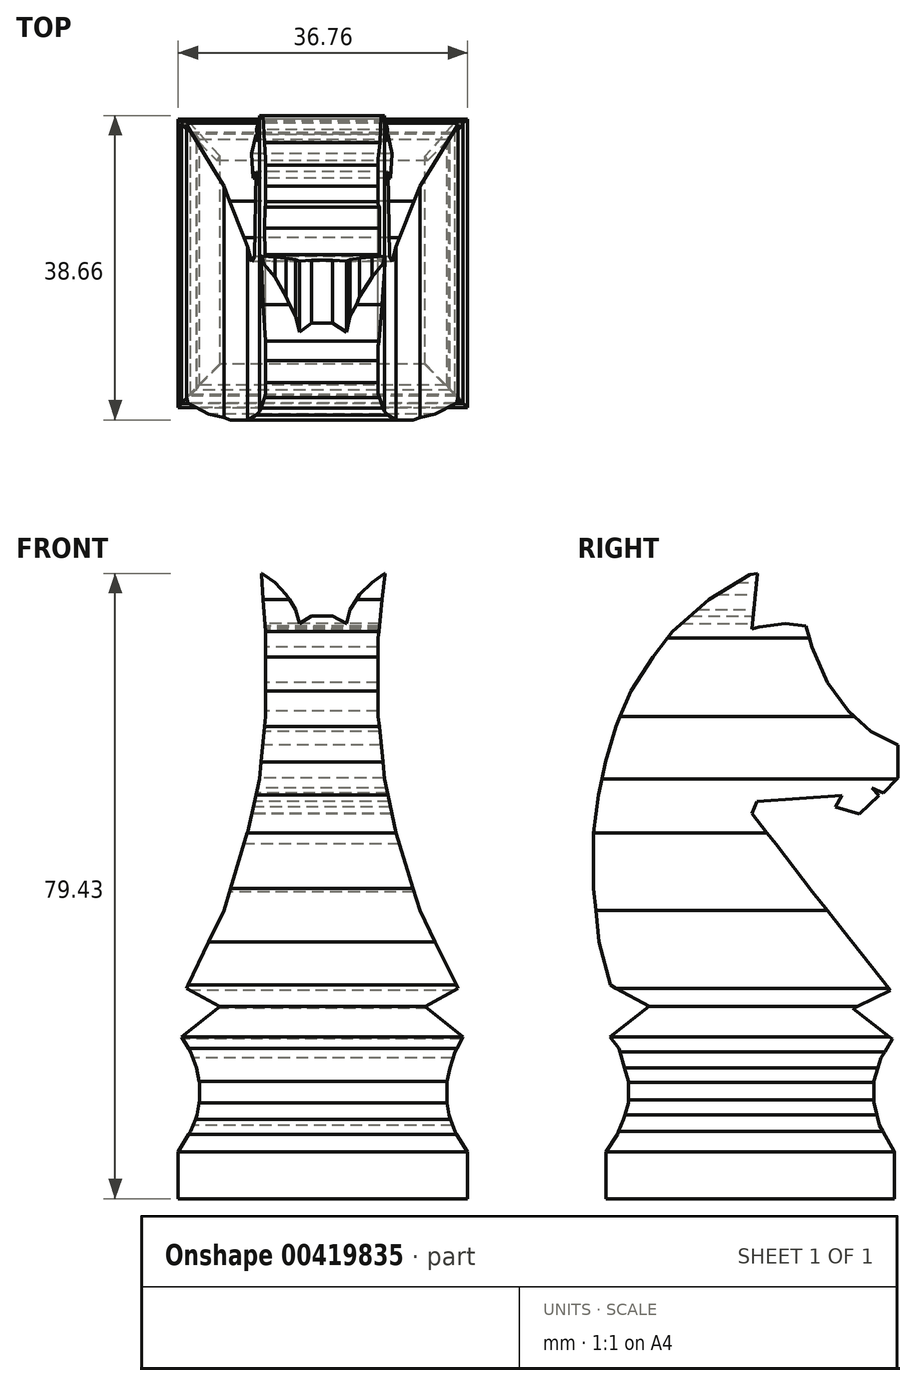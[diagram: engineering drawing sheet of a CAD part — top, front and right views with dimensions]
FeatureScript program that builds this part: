
annotation { "Feature Type Name" : "Feature", "Feature Type Description" : "" }
export const myFeature = defineFeature(function(context is Context, id is Id, definition is map)
    precondition{}
    {
        {
            var Q0;
            Q0=qCreatedBy(makeId("Front.planeOp"),FACE);
            var sketch = newSketch(context, id + "F0", { "sketchPlane" : qUnion([Q0])});
            skSolve(sketch);
        }
        {
            var Q0;
            Q0=qCreatedBy(makeId("Right.planeOp"),FACE);
            var sketch = newSketch(context, id + "F1", { "sketchPlane" : qUnion([Q0])});
            skSolve(sketch);
        }
        {
            var Q0;
            Q0=qCreatedBy(makeId("Right.planeOp"),FACE);
            var sketch = newSketch(context, id + "F2", { "sketchPlane" : qUnion([Q0])});
            skLineSegment(sketch, "E0.bottom", {"start": v(21.59, 43.18) * mm, "end": v(-21.6, 43.18) * mm});
            skLineSegment(sketch, "E0.top", {"start": v(21.6, -43.18) * mm, "end": v(-21.59, -43.18) * mm});
            skLineSegment(sketch, "E0.left", {"start": v(21.59, 43.18) * mm, "end": v(21.6, -43.18) * mm});
            skLineSegment(sketch, "E0.right", {"start": v(-21.6, 43.18) * mm, "end": v(-21.59, -43.18) * mm});
            skSolve(sketch);
        }
        {
            var Q0;
            Q0 = qSketchRegion(id + "F2", true);
            extrude(context, id + "F3", {"entities" : qUnion([Q0]), "endBound" : BoundingType.SYMMETRIC, "depth" : 43.18 * mm});
        }
        {
            var Q0;
            Q0=makeQuery(id+"F3.opExtrude","SWEPT_FACE",FACE,{"disambiguationData":[OSD([sQuery(id+"F2.wireOp",EDGE,"E0.left")])]});
            var sketch = newSketch(context, id + "F4", { "sketchPlane" : qUnion([Q0])});
            skLineSegment(sketch, "E1", {"start": v(-21.59, -43.18) * mm, "end": v(21.59, -43.18) * mm});
            skLineSegment(sketch, "E2", {"start": v(21.59, -43.18) * mm, "end": v(21.59, 43.18) * mm});
            skLineSegment(sketch, "E3", {"start": v(21.59, 43.18) * mm, "end": v(-21.59, 43.18) * mm});
            skLineSegment(sketch, "E4", {"start": v(-21.59, 43.18) * mm, "end": v(-21.59, -43.18) * mm});
            skLineSegment(sketch, "E5", {"start": v(-18.46, -40.66) * mm, "end": v(18.3, -40.66) * mm});
            skLineSegment(sketch, "E6", {"start": v(18.3, -40.66) * mm, "end": v(18.3, -34.69) * mm});
            skLineSegment(sketch, "E7", {"start": v(18.3, -34.69) * mm, "end": v(16.76, -32.12) * mm});
            skLineSegment(sketch, "E8", {"start": v(16.76, -32.12) * mm, "end": v(15.89, -30.04) * mm});
            skLineSegment(sketch, "E9", {"start": v(15.89, -30.04) * mm, "end": v(15.6, -28.1) * mm});
            skLineSegment(sketch, "E10", {"start": v(15.6, -28.1) * mm, "end": v(15.6, -25.91) * mm});
            skLineSegment(sketch, "E11", {"start": v(15.6, -25.91) * mm, "end": v(15.99, -24.03) * mm});
            skLineSegment(sketch, "E12", {"start": v(15.99, -24.03) * mm, "end": v(16.73, -22) * mm});
            skLineSegment(sketch, "E13", {"start": v(16.73, -22) * mm, "end": v(17.9, -20.1) * mm});
            skLineSegment(sketch, "E14", {"start": v(17.9, -20.1) * mm, "end": v(13.01, -16.24) * mm});
            skLineSegment(sketch, "E15", {"start": v(13.01, -16.24) * mm, "end": v(17.27, -13.92) * mm});
            skLineSegment(sketch, "E16", {"start": v(17.27, -13.92) * mm, "end": v(12.51, -4.06) * mm});
            skLineSegment(sketch, "E17", {"start": v(12.51, -4.06) * mm, "end": v(9.52, 5.8) * mm});
            skLineSegment(sketch, "E18", {"start": v(9.52, 5.8) * mm, "end": v(7.96, 12.63) * mm});
            skLineSegment(sketch, "E19", {"start": v(7.96, 12.63) * mm, "end": v(7.18, 20.62) * mm});
            skLineSegment(sketch, "E20", {"start": v(7.18, 20.62) * mm, "end": v(7.18, 30.56) * mm});
            skLineSegment(sketch, "E21", {"start": v(7.18, 30.56) * mm, "end": v(7.74, 38.8) * mm});
            skLineSegment(sketch, "E22", {"start": v(7.74, 38.8) * mm, "end": v(5.98, 37.6) * mm});
            skLineSegment(sketch, "E23", {"start": v(5.98, 37.6) * mm, "end": v(4.59, 36.11) * mm});
            skLineSegment(sketch, "E24", {"start": v(4.59, 36.11) * mm, "end": v(3.38, 34.2) * mm});
            skLineSegment(sketch, "E25", {"start": v(3.38, 34.2) * mm, "end": v(2.9, 32.38) * mm});
            skLineSegment(sketch, "E26", {"start": v(2.9, 32.38) * mm, "end": v(1.37, 33.38) * mm});
            skLineSegment(sketch, "E27", {"start": v(1.37, 33.38) * mm, "end": v(-1.3, 33.38) * mm});
            skLineSegment(sketch, "E28", {"start": v(-1.3, 33.38) * mm, "end": v(-3.05, 32.38) * mm});
            skLineSegment(sketch, "E29", {"start": v(-3.05, 32.38) * mm, "end": v(-3.53, 34.2) * mm});
            skLineSegment(sketch, "E30", {"start": v(-3.53, 34.2) * mm, "end": v(-4.7, 36.11) * mm});
            skLineSegment(sketch, "E31", {"start": v(-4.7, 36.11) * mm, "end": v(-6.3, 37.6) * mm});
            skLineSegment(sketch, "E32", {"start": v(-6.3, 37.6) * mm, "end": v(-7.95, 38.8) * mm});
            skLineSegment(sketch, "E33", {"start": v(-7.95, 38.8) * mm, "end": v(-7.1, 30.56) * mm});
            skLineSegment(sketch, "E34", {"start": v(-7.1, 30.56) * mm, "end": v(-7.1, 20.62) * mm});
            skLineSegment(sketch, "E35", {"start": v(-7.1, 20.62) * mm, "end": v(-7.92, 12.63) * mm});
            skLineSegment(sketch, "E36", {"start": v(-7.92, 12.63) * mm, "end": v(-9.38, 5.8) * mm});
            skLineSegment(sketch, "E37", {"start": v(-9.38, 5.8) * mm, "end": v(-12.4, -4.06) * mm});
            skLineSegment(sketch, "E38", {"start": v(-12.4, -4.06) * mm, "end": v(-17.2, -13.92) * mm});
            skLineSegment(sketch, "E39", {"start": v(-17.2, -13.92) * mm, "end": v(-13.05, -16.24) * mm});
            skLineSegment(sketch, "E40", {"start": v(-13.05, -16.24) * mm, "end": v(-17.89, -20.1) * mm});
            skLineSegment(sketch, "E41", {"start": v(-17.89, -20.1) * mm, "end": v(-16.85, -22) * mm});
            skLineSegment(sketch, "E42", {"start": v(-16.85, -22) * mm, "end": v(-16.2, -24.03) * mm});
            skLineSegment(sketch, "E43", {"start": v(-16.2, -24.03) * mm, "end": v(-15.8, -25.91) * mm});
            skLineSegment(sketch, "E44", {"start": v(-15.8, -25.91) * mm, "end": v(-15.8, -28.1) * mm});
            skLineSegment(sketch, "E45", {"start": v(-15.8, -28.1) * mm, "end": v(-16.07, -30.04) * mm});
            skLineSegment(sketch, "E46", {"start": v(-16.07, -30.04) * mm, "end": v(-16.83, -32.12) * mm});
            skLineSegment(sketch, "E47", {"start": v(-16.83, -32.12) * mm, "end": v(-18.44, -34.69) * mm});
            skLineSegment(sketch, "E48", {"start": v(-18.44, -34.69) * mm, "end": v(-18.46, -40.66) * mm});
            skSolve(sketch);
        }
        {
            var Q0;
            Q0=makeQuery(id+"F4.imprint","IMPRINT",FACE,{"disambiguationData":[TD([[makeQuery(id+"F4.imprint","IMPRINT",EDGE,{"derivedFrom":sQuery(id+"F4.wireOp",EDGE,"E1")}),1.0]])]});
            extrude(context, id + "F5", {"entities" : qUnion([Q0]), "operationType" : NewBodyOperationType.REMOVE, "oppositeDirection" : true, "depth" : 43.18 * mm});
        }
        {
            var Q0;
            Q0=qCreatedBy(makeId("Right.planeOp"),FACE);
            var sketch = newSketch(context, id + "F6", { "sketchPlane" : qUnion([Q0])});
            skLineSegment(sketch, "E49", {"start": v(22.04, -40.82) * mm, "end": v(18.95, -40.82) * mm});
            skLineSegment(sketch, "E50", {"start": v(18.95, -40.82) * mm, "end": v(18.95, -34.69) * mm});
            skLineSegment(sketch, "E51", {"start": v(18.95, -34.69) * mm, "end": v(17.04, -31.36) * mm});
            skLineSegment(sketch, "E52", {"start": v(17.04, -31.36) * mm, "end": v(16.36, -28.41) * mm});
            skLineSegment(sketch, "E53", {"start": v(16.36, -28.41) * mm, "end": v(16.36, -25.69) * mm});
            skLineSegment(sketch, "E54", {"start": v(16.36, -25.69) * mm, "end": v(17.25, -22.75) * mm});
            skLineSegment(sketch, "E55", {"start": v(17.25, -22.75) * mm, "end": v(18.7, -20.4) * mm});
            skLineSegment(sketch, "E56", {"start": v(18.7, -20.4) * mm, "end": v(13.68, -16.51) * mm});
            skLineSegment(sketch, "E57", {"start": v(13.68, -16.51) * mm, "end": v(18.45, -14.18) * mm});
            skLineSegment(sketch, "E58", {"start": v(18.45, -14.18) * mm, "end": v(12.48, -6.63) * mm});
            skLineSegment(sketch, "E59", {"start": v(12.48, -6.63) * mm, "end": v(8.52, -1.68) * mm});
            skLineSegment(sketch, "E60", {"start": v(8.52, -1.68) * mm, "end": v(3.89, 4.38) * mm});
            skLineSegment(sketch, "E61", {"start": v(3.89, 4.38) * mm, "end": v(0.83, 8.24) * mm});
            skLineSegment(sketch, "E62", {"start": v(0.83, 8.24) * mm, "end": v(1.45, 9.81) * mm});
            skLineSegment(sketch, "E63", {"start": v(1.45, 9.81) * mm, "end": v(12.28, 10.55) * mm});
            skLineSegment(sketch, "E64", {"start": v(12.28, 10.55) * mm, "end": v(11.47, 9.1) * mm});
            skLineSegment(sketch, "E65", {"start": v(11.47, 9.1) * mm, "end": v(14.53, 8.23) * mm});
            skLineSegment(sketch, "E66", {"start": v(14.53, 8.23) * mm, "end": v(16.98, 10.58) * mm});
            skLineSegment(sketch, "E67", {"start": v(16.98, 10.58) * mm, "end": v(16.07, 11.53) * mm});
            skLineSegment(sketch, "E68", {"start": v(16.07, 11.53) * mm, "end": v(17.57, 10.85) * mm});
            skLineSegment(sketch, "E69", {"start": v(17.57, 10.85) * mm, "end": v(19.39, 12.78) * mm});
            skLineSegment(sketch, "E70", {"start": v(19.39, 12.78) * mm, "end": v(19.39, 16.97) * mm});
            skLineSegment(sketch, "E71", {"start": v(19.39, 16.97) * mm, "end": v(15.96, 18.72) * mm});
            skLineSegment(sketch, "E72", {"start": v(15.96, 18.72) * mm, "end": v(13.1, 21.3) * mm});
            skLineSegment(sketch, "E73", {"start": v(13.1, 21.3) * mm, "end": v(10.42, 24.93) * mm});
            skLineSegment(sketch, "E74", {"start": v(10.42, 24.93) * mm, "end": v(8.47, 29.44) * mm});
            skLineSegment(sketch, "E75", {"start": v(8.47, 29.44) * mm, "end": v(7.73, 32.1) * mm});
            skLineSegment(sketch, "E76", {"start": v(7.73, 32.1) * mm, "end": v(5.08, 32.39) * mm});
            skLineSegment(sketch, "E77", {"start": v(5.08, 32.39) * mm, "end": v(1.72, 31.96) * mm});
            skLineSegment(sketch, "E78", {"start": v(1.72, 31.96) * mm, "end": v(0.87, 31.73) * mm});
            skLineSegment(sketch, "E79", {"start": v(0.87, 31.73) * mm, "end": v(1.53, 38.77) * mm});
            skLineSegment(sketch, "E80", {"start": v(1.53, 38.77) * mm, "end": v(0.57, 38.63) * mm});
            skLineSegment(sketch, "E81", {"start": v(0.57, 38.63) * mm, "end": v(-4.64, 35.47) * mm});
            skLineSegment(sketch, "E82", {"start": v(-4.64, 35.47) * mm, "end": v(-9.25, 31.4) * mm});
            skLineSegment(sketch, "E83", {"start": v(-9.25, 31.4) * mm, "end": v(-11.72, 28.13) * mm});
            skLineSegment(sketch, "E84", {"start": v(-11.72, 28.13) * mm, "end": v(-14.5, 23.83) * mm});
            skLineSegment(sketch, "E85", {"start": v(-14.5, 23.83) * mm, "end": v(-16.46, 19.35) * mm});
            skLineSegment(sketch, "E86", {"start": v(-16.46, 19.35) * mm, "end": v(-17.76, 14.79) * mm});
            skLineSegment(sketch, "E87", {"start": v(-17.76, 14.79) * mm, "end": v(-18.65, 10.64) * mm});
            skLineSegment(sketch, "E88", {"start": v(-18.65, 10.64) * mm, "end": v(-19.27, 5.77) * mm});
            skLineSegment(sketch, "E89", {"start": v(-19.27, 5.77) * mm, "end": v(-19.27, -1.27) * mm});
            skLineSegment(sketch, "E90", {"start": v(-19.27, -1.27) * mm, "end": v(-18.56, -8.03) * mm});
            skLineSegment(sketch, "E91", {"start": v(-18.56, -8.03) * mm, "end": v(-17.11, -13.53) * mm});
            skLineSegment(sketch, "E92", {"start": v(-17.11, -13.53) * mm, "end": v(-12.2, -16.21) * mm});
            skLineSegment(sketch, "E93", {"start": v(-12.2, -16.21) * mm, "end": v(-17.2, -20.09) * mm});
            skLineSegment(sketch, "E94", {"start": v(-17.2, -20.09) * mm, "end": v(-16.06, -21.55) * mm});
            skLineSegment(sketch, "E95", {"start": v(-16.06, -21.55) * mm, "end": v(-14.86, -25.77) * mm});
            skLineSegment(sketch, "E96", {"start": v(-14.86, -25.77) * mm, "end": v(-14.86, -28.47) * mm});
            skLineSegment(sketch, "E97", {"start": v(-14.86, -28.47) * mm, "end": v(-15.46, -30.57) * mm});
            skLineSegment(sketch, "E98", {"start": v(-15.46, -30.57) * mm, "end": v(-16.25, -32.49) * mm});
            skLineSegment(sketch, "E99", {"start": v(-16.25, -32.49) * mm, "end": v(-17.68, -34.69) * mm});
            skLineSegment(sketch, "E100", {"start": v(-17.68, -34.69) * mm, "end": v(-17.68, -40.68) * mm});
            skLineSegment(sketch, "E101", {"start": v(-17.68, -40.68) * mm, "end": v(-21.88, -40.68) * mm});
            skLineSegment(sketch, "E102", {"start": v(-21.88, -40.68) * mm, "end": v(-21.88, 40.47) * mm});
            skLineSegment(sketch, "E103", {"start": v(-21.88, 40.47) * mm, "end": v(22.18, 40.47) * mm});
            skLineSegment(sketch, "E104", {"start": v(22.18, 40.47) * mm, "end": v(22.04, -40.82) * mm});
            skSolve(sketch);
        }
        {
            var Q0;
            Q0=makeQuery(id+"F6.imprint","IMPRINT",FACE,{"disambiguationData":[TD([[makeQuery(id+"F6.imprint","IMPRINT",EDGE,{"derivedFrom":sQuery(id+"F6.wireOp",EDGE,"E49")}),-1.0]])]});
            extrude(context, id + "F7", {"entities" : qUnion([Q0]), "operationType" : NewBodyOperationType.REMOVE, "endBound" : BoundingType.SYMMETRIC, "depth" : 43.18 * mm});
        }
    });
